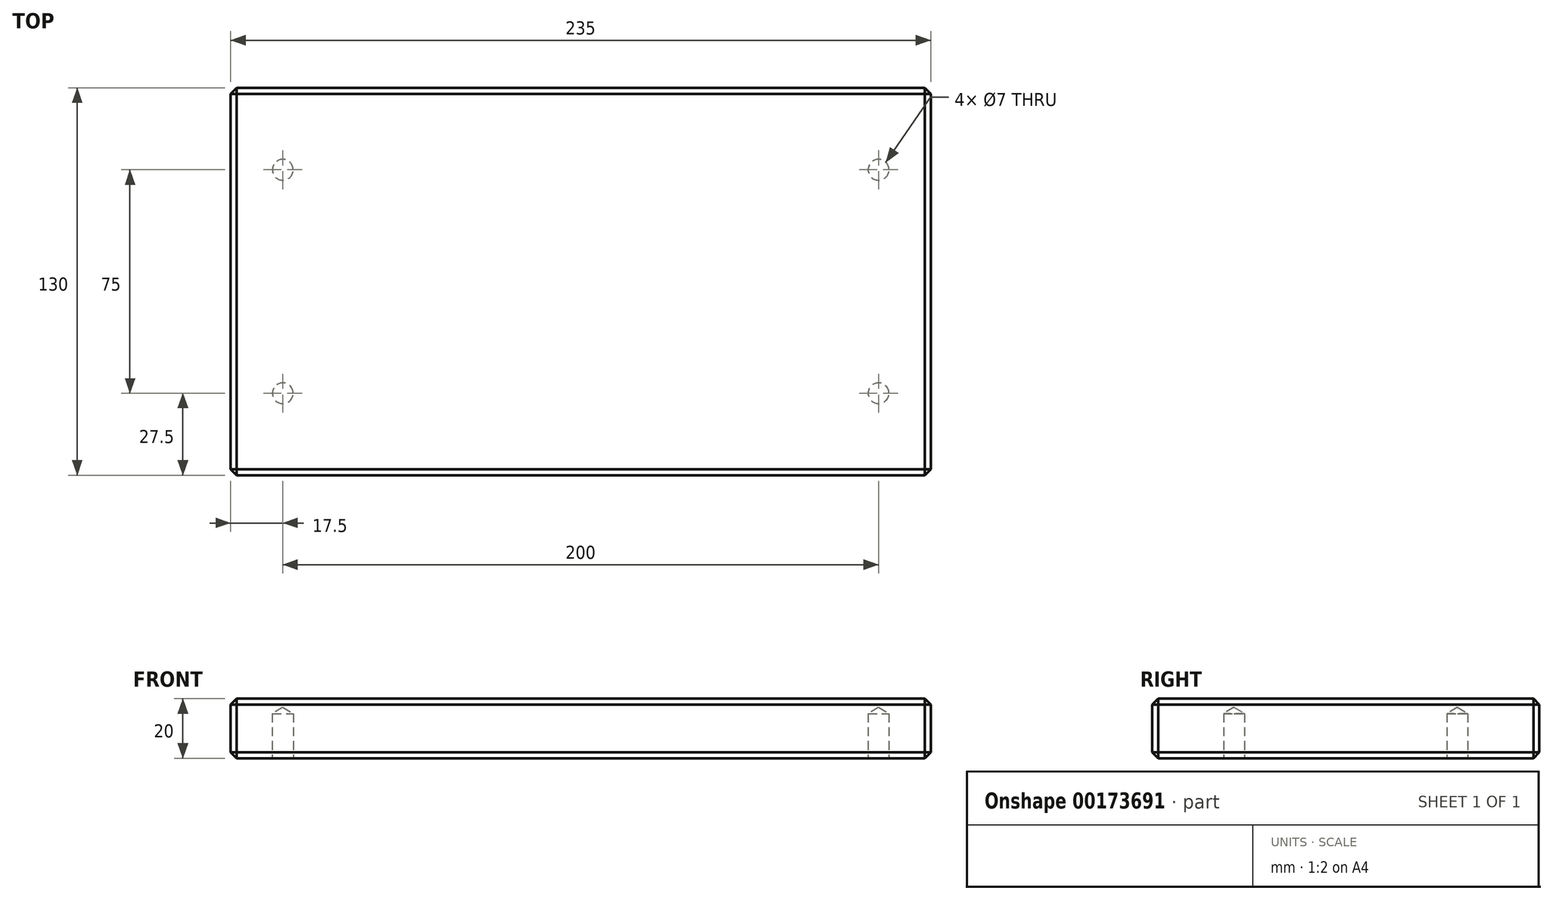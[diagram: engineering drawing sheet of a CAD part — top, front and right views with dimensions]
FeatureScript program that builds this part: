
annotation { "Feature Type Name" : "Feature", "Feature Type Description" : "" }
export const myFeature = defineFeature(function(context is Context, id is Id, definition is map)
    precondition{}
    {
        {
            var Q0;
            Q0=qCreatedBy(makeId("Top.planeOp"),FACE);
            var sketch = newSketch(context, id + "F0", { "sketchPlane" : qUnion([Q0])});
            skLineSegment(sketch, "E0.bottom", {"start": v(-117.5, -65) * mm, "end": v(117.5, -65) * mm});
            skLineSegment(sketch, "E0.top", {"start": v(-117.5, 65) * mm, "end": v(117.5, 65) * mm});
            skLineSegment(sketch, "E0.left", {"start": v(-117.5, -65) * mm, "end": v(-117.5, 65) * mm});
            skLineSegment(sketch, "E0.right", {"start": v(117.5, -65) * mm, "end": v(117.5, 65) * mm});
            skPoint(sketch, "E0.middle", {"position": v(0, 0) * mm});
            skSolve(sketch);
        }
        {
            var Q0;
            Q0=qSketchRegion(id+"F0",true);
            extrude(context, id + "F1", {"entities" : qUnion([Q0]), "depth" : 20 * mm});
        }
        {
            var Q0;
            Q0=makeQuery(id+"F1.opExtrude","SWEPT_FACE",FACE,{"disambiguationData":[OSD([sQuery(id+"F0.wireOp",EDGE,"E0.bottom")])]});
            var Q1;
            Q1=makeQuery(id+"F1.opExtrude","SWEPT_FACE",FACE,{"disambiguationData":[OSD([sQuery(id+"F0.wireOp",EDGE,"E0.right")])]});
            var Q2;
            Q2=makeQuery(id+"F1.opExtrude","SWEPT_FACE",FACE,{"disambiguationData":[OSD([sQuery(id+"F0.wireOp",EDGE,"E0.top")])]});
            var Q3;
            Q3=makeQuery(id+"F1.opExtrude","SWEPT_FACE",FACE,{"disambiguationData":[OSD([sQuery(id+"F0.wireOp",EDGE,"E0.left")])]});
            chamfer(context, id + "F2", {"entities" : qUnion([Q0, Q1, Q2, Q3]), "width" : 2 * mm, "tangentPropagation" : true});
        }
        {
            var Q0;
            Q0=makeQuery(id+"F1.opExtrude","CAP_FACE",FACE,{"disambiguationData":[OSD([sQuery(id+"F0.wireOp",EDGE,"E0.bottom"),sQuery(id+"F0.wireOp",EDGE,"E0.top"),sQuery(id+"F0.wireOp",EDGE,"E0.left"),sQuery(id+"F0.wireOp",EDGE,"E0.right")])],"isStart":true});
            var sketch = newSketch(context, id + "F3", { "sketchPlane" : qUnion([Q0])});
            skPoint(sketch, "E1", {"position": v(-100, -37.5) * mm});
            skLineSegment(sketch, "E2", {"start": v(0, 0) * mm, "end": v(0, 36.1) * mm, "construction": true});
            skPoint(sketch, "E3.MirrorP", {"position": v(100, -37.5) * mm});
            skLineSegment(sketch, "E4", {"start": v(0, 0) * mm, "end": v(-44.95, 0) * mm, "construction": true});
            skPoint(sketch, "E5.MirrorP", {"position": v(-100, 37.5) * mm});
            skPoint(sketch, "E6.MirrorP", {"position": v(100, 37.5) * mm});
            skSolve(sketch);
        }
        {
            var Q0;
            Q0=sQuery(id+"F3.wireOp",VERTEX,"E1");
            var Q1;
            Q1=sQuery(id+"F3.wireOp",VERTEX,"E3.MirrorP");
            var Q2;
            Q2=sQuery(id+"F3.wireOp",VERTEX,"E5.MirrorP");
            var Q3;
            Q3=sQuery(id+"F3.wireOp",VERTEX,"E6.MirrorP");
            var Q4;
            Q4=makeQuery(id+"F1.opExtrude","SWEPT_BODY",BODY,{"disambiguationData":[OSD([sQuery(id+"F0.wireOp",EDGE,"E0.bottom"),sQuery(id+"F0.wireOp",EDGE,"E0.top"),sQuery(id+"F0.wireOp",EDGE,"E0.left"),sQuery(id+"F0.wireOp",EDGE,"E0.right")])]});
            hole(context, id + "F4", {"style" : HoleStyle.SIMPLE, "endStyle" : HoleEndStyle.BLIND, "standardTappedOrClearance" : lookupTablePath({ "standard" : "ISO", "engagement" : "75%", "pitch" : "1 mm", "size" : "M8", "type" : "Tapped" }), "standardBlindInLast" : lookupTablePath({ "standard" : "ISO", "engagement" : "75%", "pitch" : "1 mm", "size" : "M8", "type" : "Tapped" }), "holeDiameter" : 7 * mm, "holeDepth" : 15 * mm, "locations" : qUnion([Q0, Q1, Q2, Q3]), "scope" : qUnion([Q4]), "majorDiameter" : 8 * mm});
        }
    });
